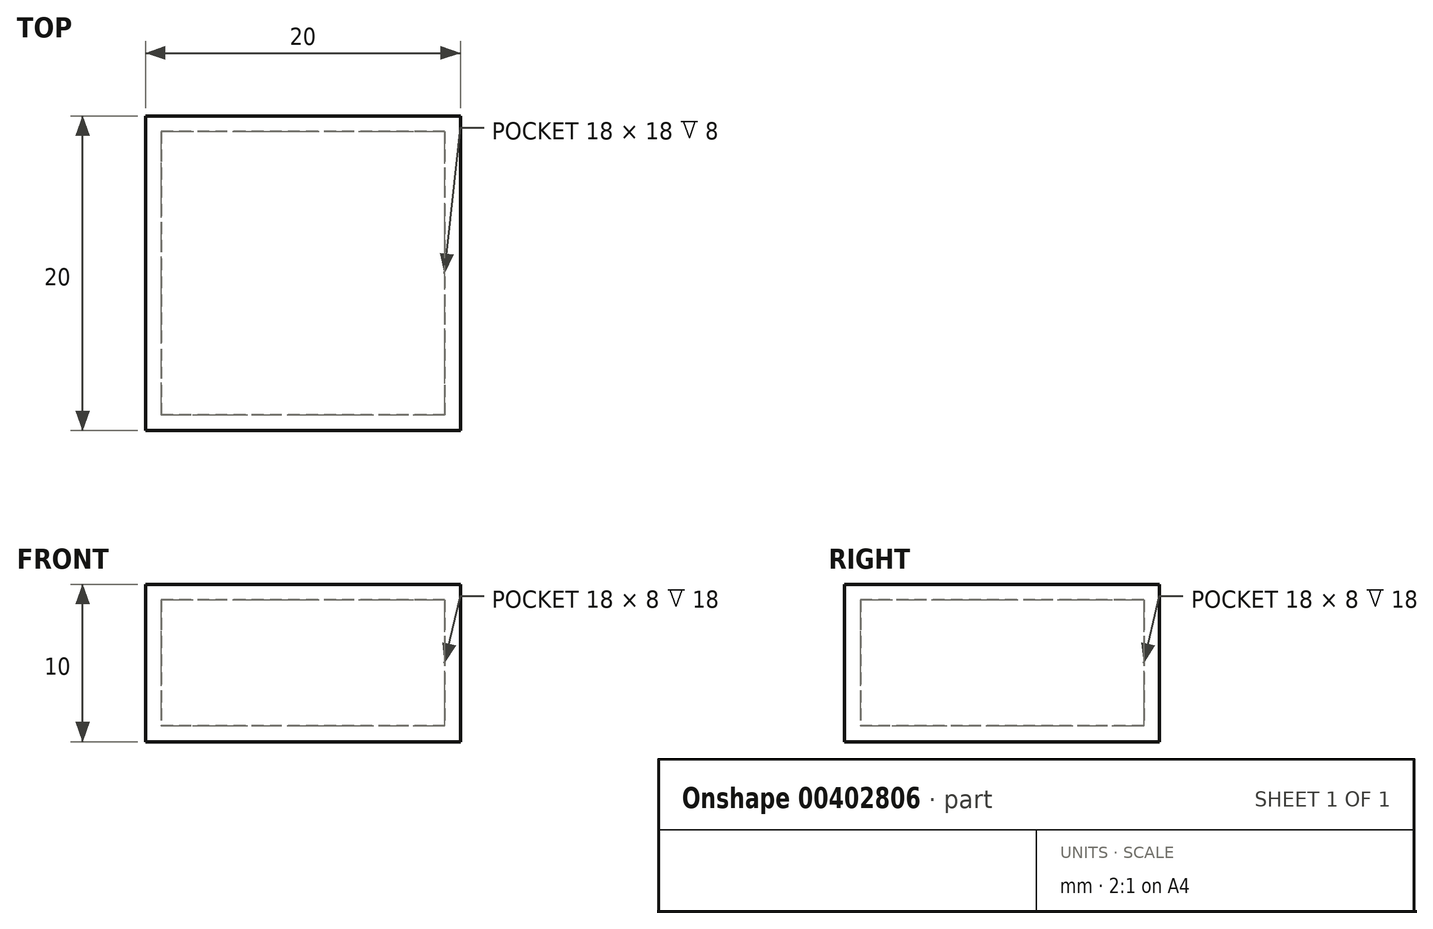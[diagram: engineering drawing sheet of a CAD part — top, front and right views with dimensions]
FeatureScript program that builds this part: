
annotation { "Feature Type Name" : "Feature", "Feature Type Description" : "" }
export const myFeature = defineFeature(function(context is Context, id is Id, definition is map)
    precondition{}
    {
        {
            var Q0;
            Q0=qCreatedBy(makeId("Top.planeOp"),FACE);
            var sketch = newSketch(context, id + "F0", { "sketchPlane" : qUnion([Q0])});
            skLineSegment(sketch, "E0.bottom", {"start": v(10, 10) * mm, "end": v(-10, 10) * mm});
            skLineSegment(sketch, "E0.top", {"start": v(10, -10) * mm, "end": v(-10, -10) * mm});
            skLineSegment(sketch, "E0.left", {"start": v(10, 10) * mm, "end": v(10, -10) * mm});
            skLineSegment(sketch, "E0.right", {"start": v(-10, 10) * mm, "end": v(-10, -10) * mm});
            skPoint(sketch, "E0.middle", {"position": v(0, 0) * mm});
            skSolve(sketch);
        }
        {
            var Q0;
            Q0=makeQuery(id+"F0.imprint","IMPRINT",FACE,{"disambiguationData":[TD([[makeQuery(id+"F0.imprint","IMPRINT",EDGE,{"derivedFrom":sQuery(id+"F0.wireOp",EDGE,"E0.bottom")}),1.0]])]});
            var Q1;
            Q1=makeQuery(id+"F0.imprint","IMPRINT",FACE,{"disambiguationData":[TD([[makeQuery(id+"F0.imprint","IMPRINT",EDGE,{"derivedFrom":sQuery(id+"F0.wireOp",EDGE,"f64fba04-7fcc-42e7-be6c-53b2896c33aa.0")}),1.0]])]});
            extrude(context, id + "F1", {"entities" : qUnion([Q0, Q1]), "depth" : 10 * mm});
        }
        {
            var Q0;
            Q0=makeQuery(id+"F1.opExtrude","SWEPT_FACE",FACE,{"disambiguationData":[OSD([sQuery(id+"F0.wireOp",EDGE,"E0.top")])]});
            var Q1;
            Q1=makeQuery(id+"F1.opExtrude","SWEPT_BODY",BODY,{"disambiguationData":[OSD([sQuery(id+"F0.wireOp",EDGE,"E0.bottom"),sQuery(id+"F0.wireOp",EDGE,"E0.top"),sQuery(id+"F0.wireOp",EDGE,"E0.left"),sQuery(id+"F0.wireOp",EDGE,"E0.right")])]});
            shell(context, id + "F2", {"isHollow" : true, "entities" : qUnion([Q0]), "parts" : qUnion([Q1]), "thickness" : 1 * mm});
        }
    });
